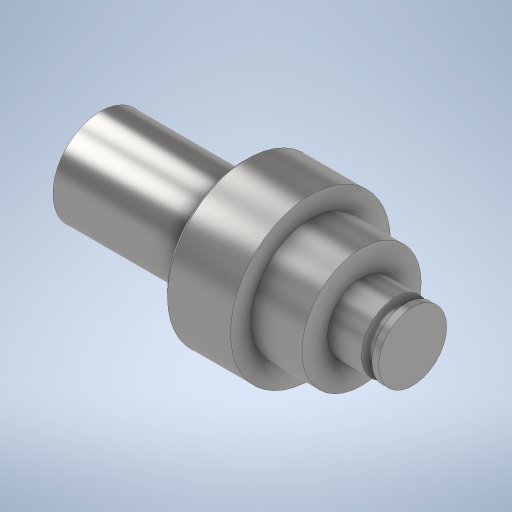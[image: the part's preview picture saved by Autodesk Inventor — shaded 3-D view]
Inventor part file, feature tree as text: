
AUTODESK INVENTOR PART (.ipt)
format: ipt  version: 2024 (Build 280153000, 153)  size: 325,632 bytes
history: native  units: mm
features: chamfer x2, revolve x1, sketch x1
ambient origin geometry x8: Origin, YZ Plane, XZ Plane, XY Plane, X Axis, Y Axis, Z Axis, Center Point
bodies: Volumenkörper1 (feature_tree)
feature tree (4):
  revolve  "Umdrehung1"
  chamfer  "Fasen1"  Distance=4.0mm
  chamfer  "Fasen2"  Distance=20.0mm
  sketch  "Skizze1"  dims[d0=184.0mm d1=4.0mm d2=20.0mm d3=30.0mm d4=40.0mm d5=40.0mm d6=30.0mm d7=84.0mm d8=56.0mm d9=94.0mm d10=70.0mm d11=90.0deg d12=4.0mm d13=2.0mm d14=1.745329mm d15=3.0mm d16=2.0mm d17=1.745329mm]
